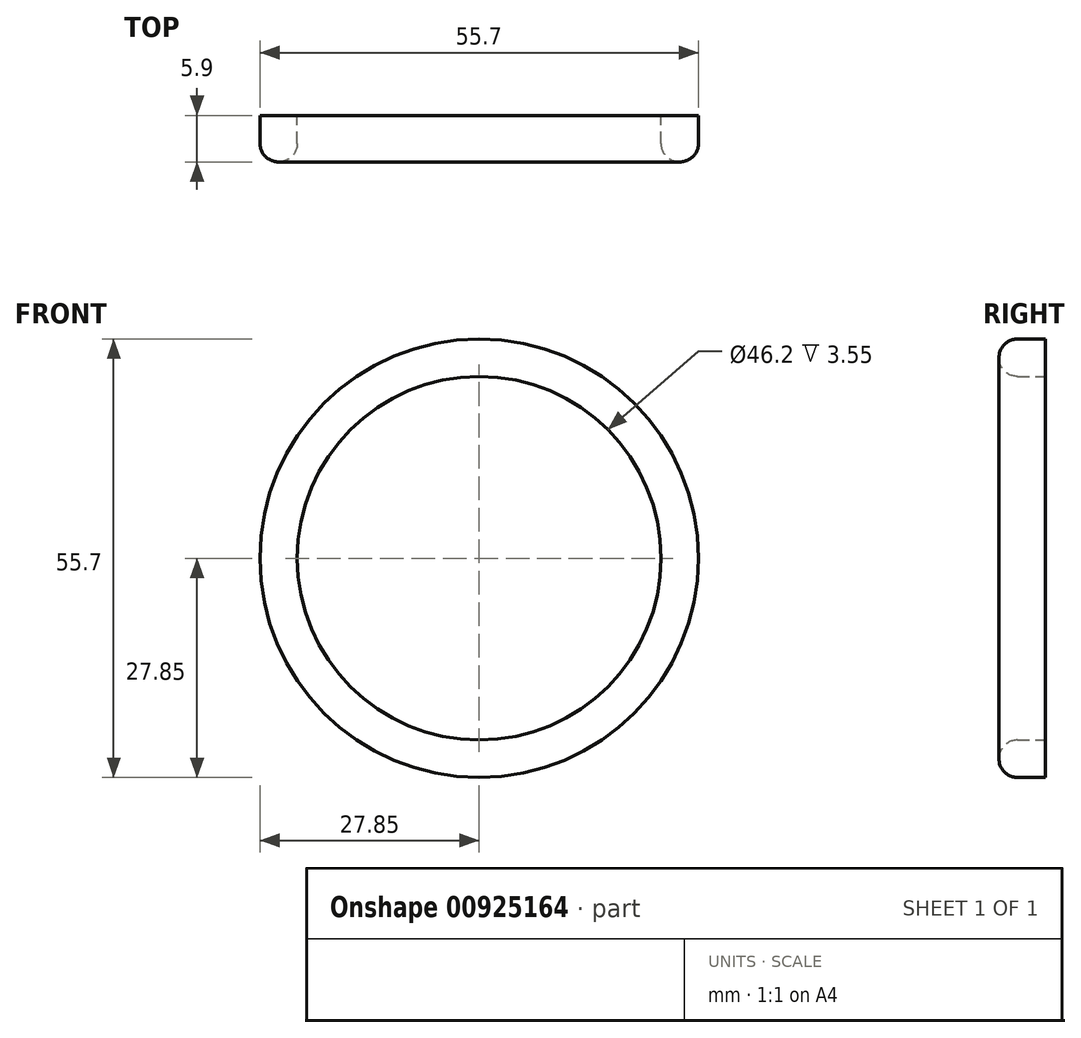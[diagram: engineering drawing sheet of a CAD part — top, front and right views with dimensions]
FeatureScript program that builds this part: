
annotation { "Feature Type Name" : "Feature", "Feature Type Description" : "" }
export const myFeature = defineFeature(function(context is Context, id is Id, definition is map)
    precondition{}
    {
        {
            var Q0;
            Q0=qCreatedBy(makeId("Right.planeOp"),FACE);
            var sketch = newSketch(context, id + "F0", { "sketchPlane" : qUnion([Q0])});
            skLineSegment(sketch, "E0", {"start": v(0, 23.1) * mm, "end": v(-3.55, 23.1) * mm});
            skLineSegment(sketch, "E1", {"start": v(-5.9, 25.45) * mm, "end": v(-5.9, 25.5) * mm});
            skLineSegment(sketch, "E2", {"start": v(-3.55, 27.85) * mm, "end": v(0, 27.85) * mm});
            skLineSegment(sketch, "E3", {"start": v(0, 27.85) * mm, "end": v(0, 23.1) * mm});
            skLineSegment(sketch, "E4", {"start": v(0, 0) * mm, "end": v(-34.42, 0) * mm, "construction": true});
            skPoint(sketch, "E5.visualSharp", {"position": v(-5.9, 27.85) * mm});
            skArc(sketch, "E5.filletArc", {"start": v(-3.55, 27.85) * mm, "mid": v(-5.21, 27.16) * mm, "end": v(-5.9, 25.5) * mm});
            skPoint(sketch, "E6.visualSharp", {"position": v(-5.9, 23.1) * mm});
            skArc(sketch, "E6.filletArc", {"start": v(-5.9, 25.45) * mm, "mid": v(-5.21, 23.79) * mm, "end": v(-3.55, 23.1) * mm});
            skSolve(sketch);
        }
        {
            var Q0;
            Q0 = qSketchRegion(id + "F0", true);
            var Q1;
            Q1=sQuery(id+"F0.wireOp",EDGE,"E4");
            revolve(context, id + "F1", {"surfaceOperationType" : NewSurfaceOperationType.NEW, "entities" : qUnion([Q0]), "axis" : qUnion([Q1]), "revolveType" : RevolveType.FULL});
        }
    });
